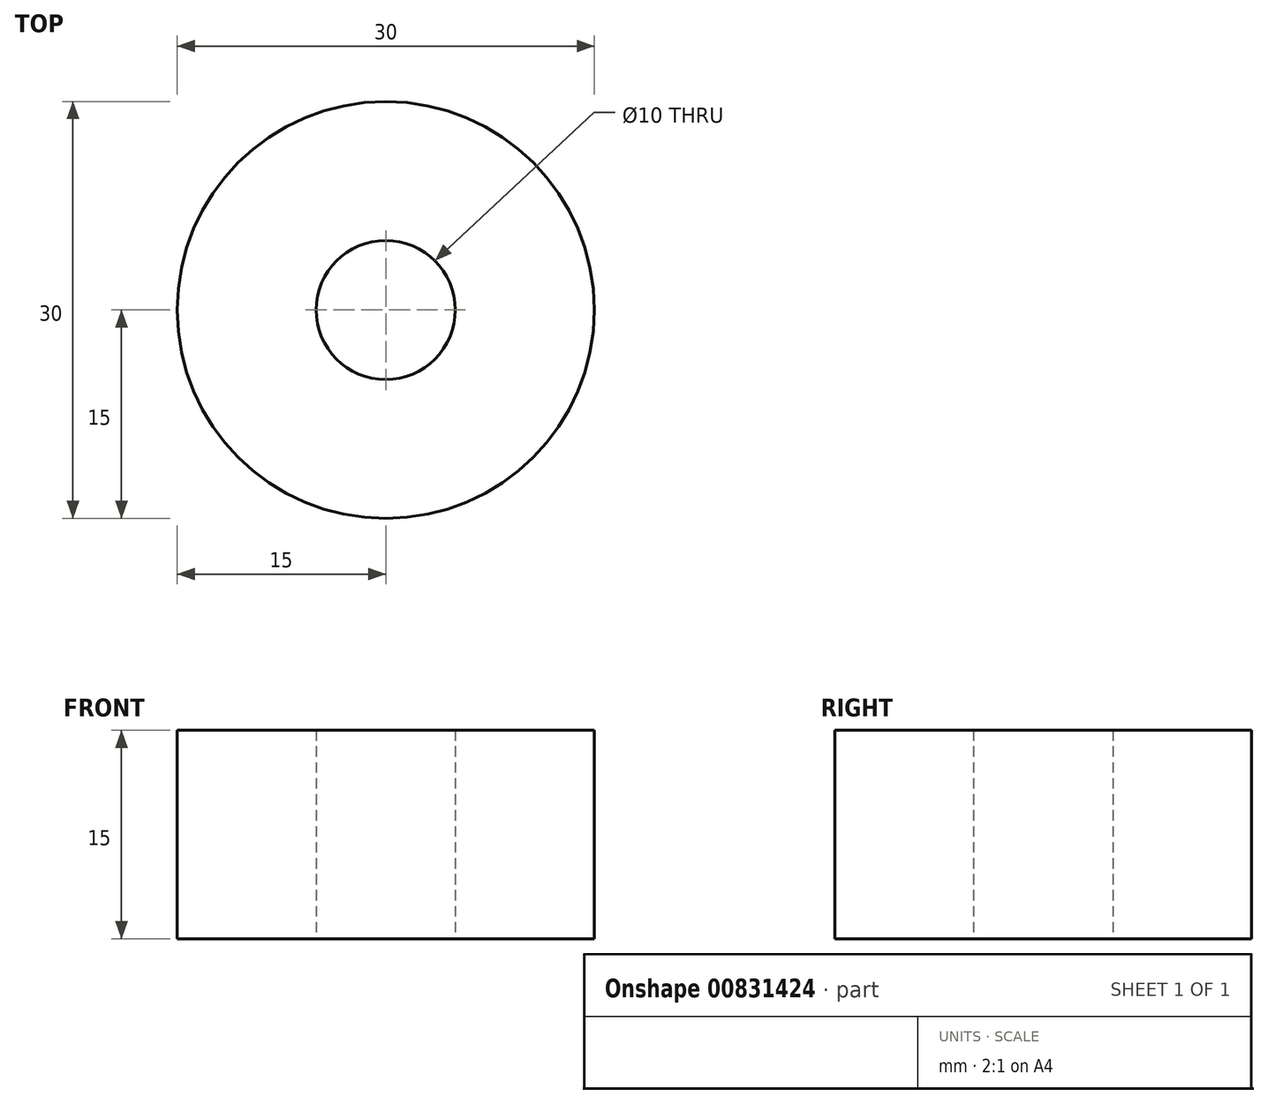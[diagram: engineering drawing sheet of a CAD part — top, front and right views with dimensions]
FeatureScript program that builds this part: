
annotation { "Feature Type Name" : "Feature", "Feature Type Description" : "" }
export const myFeature = defineFeature(function(context is Context, id is Id, definition is map)
    precondition{}
    {
        {
            var Q0;
            Q0=qCreatedBy(makeId("Top.planeOp"),FACE);
            var sketch = newSketch(context, id + "F0", { "sketchPlane" : qUnion([Q0])});
            skCircle(sketch, "E0", {"center": v(0, 0) * mm, "radius": 15 * mm});
            skSolve(sketch);
        }
        {
            var Q0;
            Q0=makeQuery(id+"F0.imprint","IMPRINT",FACE,{"disambiguationData":[TD([[makeQuery(id+"F0.imprint","IMPRINT",EDGE,{"derivedFrom":sQuery(id+"F0.wireOp",EDGE,"E0")}),1.0]])]});
            var sketch = newSketch(context, id + "F1", { "sketchPlane" : qUnion([Q0])});
            skCircle(sketch, "E1", {"center": v(0, 0) * mm, "radius": 5 * mm});
            skSolve(sketch);
        }
        {
            var Q0;
            Q0=makeQuery(id+"F0.imprint","IMPRINT",FACE,{"disambiguationData":[TD([[makeQuery(id+"F0.imprint","IMPRINT",EDGE,{"derivedFrom":sQuery(id+"F0.wireOp",EDGE,"E0")}),1.0]])]});
            extrude(context, id + "F2", {"entities" : qUnion([Q0]), "depth" : 15 * mm, "offsetDistance" : 25 * mm});
        }
        {
            var Q0;
            Q0 = qSketchRegion(id + "F1", true);
            extrude(context, id + "F3", {"entities" : qUnion([Q0]), "operationType" : NewBodyOperationType.REMOVE, "depth" : 15 * mm, "offsetDistance" : 25 * mm});
        }
    });
